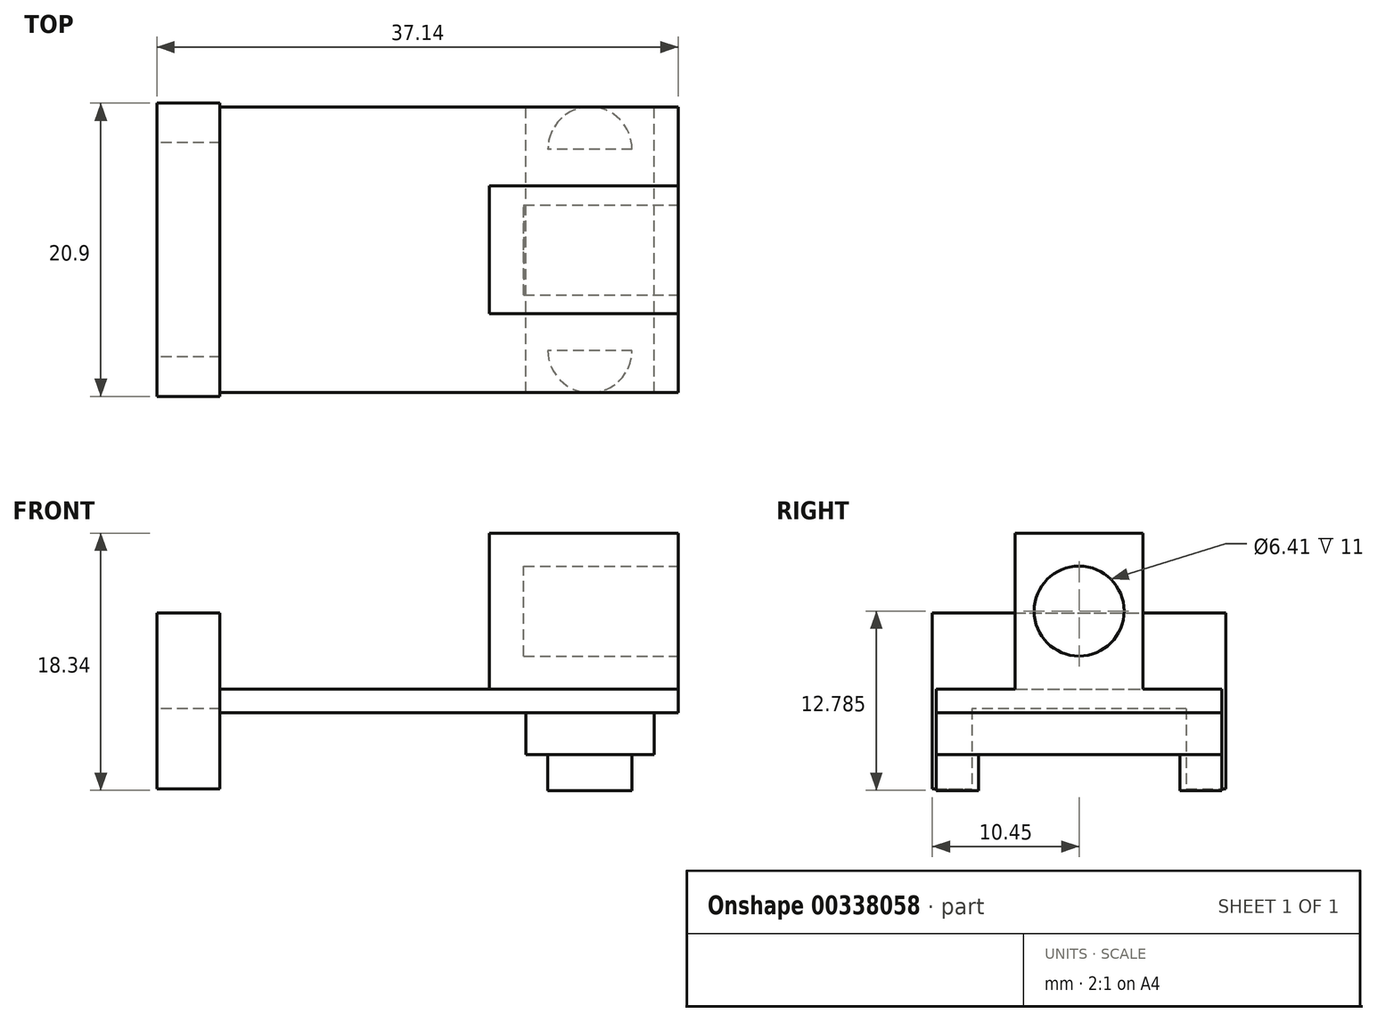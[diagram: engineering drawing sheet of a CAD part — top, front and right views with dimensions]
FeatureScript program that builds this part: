
annotation { "Feature Type Name" : "Feature", "Feature Type Description" : "" }
export const myFeature = defineFeature(function(context is Context, id is Id, definition is map)
    precondition{}
    {
        {
            var Q0;
            Q0=qCreatedBy(makeId("Top.planeOp"),FACE);
            var sketch = newSketch(context, id + "F0", { "sketchPlane" : qUnion([Q0])});
            skLineSegment(sketch, "E0.bottom", {"start": v(16.33, -10.18) * mm, "end": v(-16.33, -10.18) * mm});
            skLineSegment(sketch, "E0.top", {"start": v(16.33, 10.18) * mm, "end": v(-16.33, 10.18) * mm});
            skLineSegment(sketch, "E0.left", {"start": v(16.33, -10.18) * mm, "end": v(16.33, 10.18) * mm});
            skLineSegment(sketch, "E0.right", {"start": v(-16.33, -10.18) * mm, "end": v(-16.33, 10.18) * mm});
            skPoint(sketch, "E0.middle", {"position": v(0, 0) * mm});
            skSolve(sketch);
        }
        {
            var Q0;
            Q0=qSketchRegion(id+"F0",true);
            extrude(context, id + "F1", {"entities" : qUnion([Q0]), "endBound" : BoundingType.SYMMETRIC, "depth" : 1.71 * mm});
        }
        {
            var Q0;
            Q0=makeQuery(id+"F1.opExtrude","SWEPT_FACE",FACE,{"disambiguationData":[OSD([sQuery(id+"F0.wireOp",EDGE,"E0.right")])]});
            var sketch = newSketch(context, id + "F2", { "sketchPlane" : qUnion([Q0])});
            skLineSegment(sketch, "E1.bottom", {"start": v(10.45, -6.29) * mm, "end": v(-10.45, -6.29) * mm});
            skLineSegment(sketch, "E1.top", {"start": v(10.45, 6.29) * mm, "end": v(-10.45, 6.29) * mm});
            skLineSegment(sketch, "E1.left", {"start": v(10.45, -6.28) * mm, "end": v(10.45, 6.29) * mm});
            skLineSegment(sketch, "E1.right", {"start": v(-10.45, -6.29) * mm, "end": v(-10.45, 6.29) * mm});
            skPoint(sketch, "E1.middle", {"position": v(0, 0) * mm});
            skSolve(sketch);
        }
        {
            var Q0;
            Q0=qSketchRegion(id+"F2",true);
            extrude(context, id + "F3", {"entities" : qUnion([Q0]), "depth" : 4.48 * mm});
        }
        {
            var Q0;
            Q0=makeQuery(id+"F3.opExtrude","CAP_FACE",FACE,{"disambiguationData":[OSD([sQuery(id+"F2.wireOp",EDGE,"E1.bottom"),sQuery(id+"F2.wireOp",EDGE,"E1.top"),sQuery(id+"F2.wireOp",EDGE,"E1.left"),sQuery(id+"F2.wireOp",EDGE,"E1.right")])],"isStart":false});
            var sketch = newSketch(context, id + "F4", { "sketchPlane" : qUnion([Q0])});
            skLineSegment(sketch, "E2.bottom", {"start": v(7.64, -6.29) * mm, "end": v(-7.64, -6.29) * mm});
            skLineSegment(sketch, "E2.top", {"start": v(7.64, -0.56) * mm, "end": v(-7.64, -0.57) * mm});
            skLineSegment(sketch, "E2.left", {"start": v(7.64, -6.28) * mm, "end": v(7.64, -0.56) * mm});
            skLineSegment(sketch, "E2.right", {"start": v(-7.64, -6.29) * mm, "end": v(-7.64, -0.57) * mm});
            skPoint(sketch, "E2.middle", {"position": v(0, -3.43) * mm});
            skSolve(sketch);
        }
        {
            var Q0;
            Q0=qSketchRegion(id+"F4",true);
            extrude(context, id + "F5", {"entities" : qUnion([Q0]), "operationType" : NewBodyOperationType.REMOVE, "endBound" : BoundingType.UP_TO_NEXT, "oppositeDirection" : true, "depth" : 25 * mm});
        }
        {
            var Q0;
            Q0=makeQuery(id+"F1.opExtrude","CAP_FACE",FACE,{"disambiguationData":[OSD([sQuery(id+"F0.wireOp",EDGE,"E0.bottom"),sQuery(id+"F0.wireOp",EDGE,"E0.top"),sQuery(id+"F0.wireOp",EDGE,"E0.left"),sQuery(id+"F0.wireOp",EDGE,"E0.right")])],"isStart":true});
            var sketch = newSketch(context, id + "F6", { "sketchPlane" : qUnion([Q0])});
            skLineSegment(sketch, "E3.bottom", {"start": v(14.62, 10.18) * mm, "end": v(5.47, 10.18) * mm});
            skLineSegment(sketch, "E3.top", {"start": v(14.62, -10.18) * mm, "end": v(5.47, -10.18) * mm});
            skLineSegment(sketch, "E3.left", {"start": v(14.62, 10.18) * mm, "end": v(14.62, -10.18) * mm});
            skLineSegment(sketch, "E3.right", {"start": v(5.47, 10.18) * mm, "end": v(5.47, -10.18) * mm});
            skPoint(sketch, "E4", {"position": v(14.62, 0) * mm});
            skSolve(sketch);
        }
        {
            var Q0;
            Q0=qSketchRegion(id+"F6",true);
            extrude(context, id + "F7", {"entities" : qUnion([Q0]), "depth" : 2.97 * mm});
        }
        {
            var Q0;
            Q0=makeQuery(id+"F7.opExtrude","CAP_FACE",FACE,{"disambiguationData":[OSD([sQuery(id+"F6.wireOp",EDGE,"E3.bottom"),sQuery(id+"F6.wireOp",EDGE,"E3.top"),sQuery(id+"F6.wireOp",EDGE,"E3.left"),sQuery(id+"F6.wireOp",EDGE,"E3.right")])],"isStart":false});
            var sketch = newSketch(context, id + "F8", { "sketchPlane" : qUnion([Q0])});
            skArc(sketch, "E5", {"start": v(13.04, 7.18) * mm, "mid": v(10.04, 10.18) * mm, "end": v(7.04, 7.17) * mm});
            skPoint(sketch, "E5.centerSnap0", {"position": v(10.04, 10.18) * mm});
            skPoint(sketch, "E6", {"position": v(10.04, -10.18) * mm});
            skLineSegment(sketch, "E7", {"start": v(13.04, 7.18) * mm, "end": v(7.04, 7.17) * mm});
            skLineSegment(sketch, "E8", {"start": v(22.77, 0) * mm, "end": v(-28.1, 0) * mm, "construction": true});
            skPoint(sketch, "E8.startSnap0", {"position": v(14.62, 0) * mm});
            skLineSegment(sketch, "E9.MirrorCS", {"start": v(13.04, -7.18) * mm, "end": v(7.04, -7.18) * mm});
            skArc(sketch, "E10.MirrorCS", {"start": v(13.04, -7.18) * mm, "mid": v(10.04, -10.18) * mm, "end": v(7.04, -7.18) * mm});
            skSolve(sketch);
        }
        {
            var Q0;
            Q0=qSketchRegion(id+"F8",true);
            extrude(context, id + "F9", {"entities" : qUnion([Q0]), "operationType" : NewBodyOperationType.ADD, "depth" : 2.56 * mm});
        }
        {
            var Q0;
            Q0=makeQuery(id+"F1.opExtrude","SWEPT_FACE",FACE,{"disambiguationData":[OSD([sQuery(id+"F0.wireOp",EDGE,"E0.left")])]});
            var sketch = newSketch(context, id + "F10", { "sketchPlane" : qUnion([Q0])});
            skLineSegment(sketch, "E11.bottom", {"start": v(-4.55, 0.85) * mm, "end": v(4.55, 0.85) * mm});
            skLineSegment(sketch, "E11.top", {"start": v(-4.55, 11.96) * mm, "end": v(4.55, 11.96) * mm});
            skLineSegment(sketch, "E11.left", {"start": v(-4.55, 0.85) * mm, "end": v(-4.55, 11.96) * mm});
            skLineSegment(sketch, "E11.right", {"start": v(4.55, 0.85) * mm, "end": v(4.55, 11.96) * mm});
            skPoint(sketch, "E12", {"position": v(0, 11.96) * mm});
            skSolve(sketch);
        }
        {
            var Q0;
            Q0=qSketchRegion(id+"F10",true);
            extrude(context, id + "F11", {"entities" : qUnion([Q0]), "operationType" : NewBodyOperationType.ADD, "oppositeDirection" : true, "depth" : 13.46 * mm});
        }
        {
            var Q0;
            Q0=makeQuery(id+"F11.boolean.opBoolean","MERGE",FACE,{"derivedFrom":[makeQuery(id+"F1.opExtrude","SWEPT_FACE",FACE,{"disambiguationData":[OSD([sQuery(id+"F0.wireOp",EDGE,"E0.left")])]}),makeQuery(id+"F11.opExtrude","CAP_FACE",FACE,{"disambiguationData":[OSD([sQuery(id+"F10.wireOp",EDGE,"E11.bottom"),sQuery(id+"F10.wireOp",EDGE,"E11.top"),sQuery(id+"F10.wireOp",EDGE,"E11.left"),sQuery(id+"F10.wireOp",EDGE,"E11.right")])],"isStart":true})]});
            var sketch = newSketch(context, id + "F12", { "sketchPlane" : qUnion([Q0])});
            skCircle(sketch, "E13", {"center": v(0, 6.4) * mm, "radius": 3.2 * mm});
            skPoint(sketch, "E13.centerSnap0", {"position": v(4.55, 6.4) * mm});
            skSolve(sketch);
        }
        {
            var Q0;
            Q0=qSketchRegion(id+"F12",true);
            extrude(context, id + "F13", {"entities" : qUnion([Q0]), "operationType" : NewBodyOperationType.REMOVE, "oppositeDirection" : true, "depth" : 11 * mm});
        }
    });
